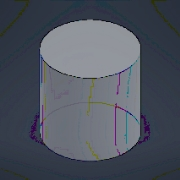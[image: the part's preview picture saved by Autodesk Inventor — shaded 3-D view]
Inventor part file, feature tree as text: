
AUTODESK INVENTOR PART (.ipt)
format: ipt  version: 2024.3 (Build 283343000, 343)  size: 134,656 bytes
history: native  units: mm
features: extrude x1, sketch x1
ambient origin geometry x8: Origin, YZ Plane, XZ Plane, XY Plane, X Axis, Y Axis, Z Axis, Center Point
bodies: Solid1 (feature_tree)
feature tree (2):
  extrude  "Extrusion1"  [1 undecoded]
  sketch  "Sketch1"  dims[d1=30.0mm d2=0.0mm]
note: 1 required parameter value undecoded (feature->parameter linkage not recoverable at this tier; creation-order binding heuristic only, values carry confidence <= 0.55)
